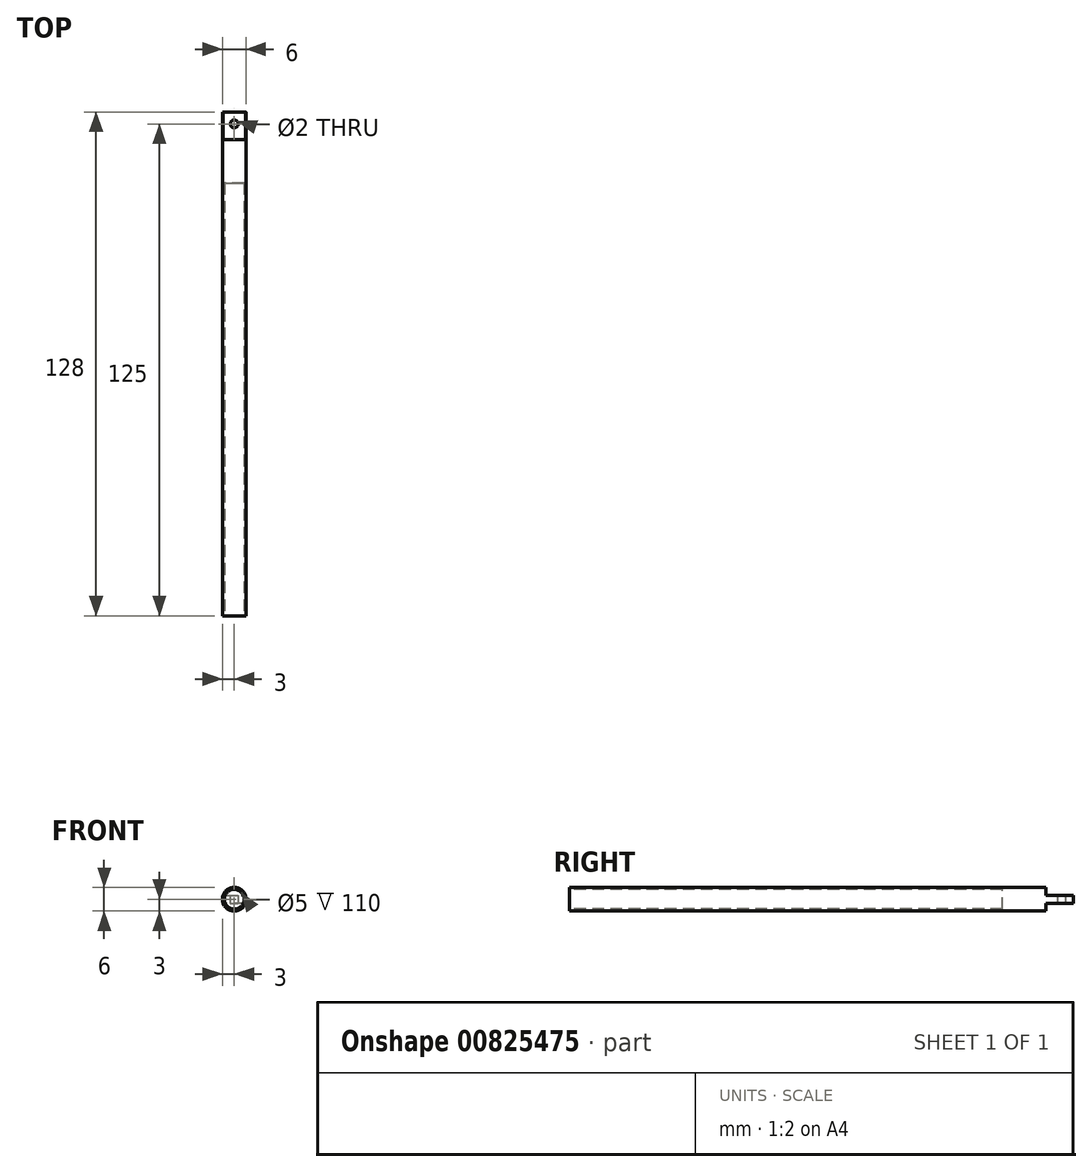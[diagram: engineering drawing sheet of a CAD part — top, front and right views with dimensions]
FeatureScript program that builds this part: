
annotation { "Feature Type Name" : "Feature", "Feature Type Description" : "" }
export const myFeature = defineFeature(function(context is Context, id is Id, definition is map)
    precondition{}
    {
        {
            var Q0;
            Q0=qCreatedBy(makeId("Front.planeOp"),FACE);
            var sketch = newSketch(context, id + "F0", { "sketchPlane" : qUnion([Q0])});
            skCircle(sketch, "E0", {"center": v(0, 0) * mm, "radius": 3 * mm});
            skSolve(sketch);
        }
        {
            var Q0;
            Q0=makeQuery(id+"F0.imprint","IMPRINT",FACE,{"disambiguationData":[TD([[makeQuery(id+"F0.imprint","IMPRINT",EDGE,{"derivedFrom":sQuery(id+"F0.wireOp",EDGE,"E0")}),1.0]])]});
            extrude(context, id + "F1", {"entities" : qUnion([Q0]), "endBound" : BoundingType.SYMMETRIC, "depth" : 128 * mm, "offsetDistance" : 25 * mm});
        }
        {
            var Q0;
            Q0=makeQuery(id+"F1.opExtrude","CAP_FACE",FACE,{"disambiguationData":[OSD([sQuery(id+"F0.wireOp",EDGE,"E0")])],"isStart":false});
            var sketch = newSketch(context, id + "F2", { "sketchPlane" : qUnion([Q0])});
            skCircle(sketch, "E1", {"center": v(0, 0) * mm, "radius": 2.5 * mm});
            skSolve(sketch);
        }
        {
            var Q0;
            Q0=makeQuery(id+"F2.imprint","IMPRINT",FACE,{"disambiguationData":[TD([[makeQuery(id+"F2.imprint","IMPRINT",EDGE,{"derivedFrom":sQuery(id+"F2.wireOp",EDGE,"E1")}),1.0]])]});
            extrude(context, id + "F3", {"entities" : qUnion([Q0]), "operationType" : NewBodyOperationType.REMOVE, "oppositeDirection" : true, "depth" : 110 * mm, "offsetDistance" : 25 * mm});
        }
        {
            var Q0;
            Q0=qCreatedBy(makeId("Right.planeOp"),FACE);
            var sketch = newSketch(context, id + "F4", { "sketchPlane" : qUnion([Q0])});
            skLineSegment(sketch, "E2.top", {"start": v(64, 1) * mm, "end": v(57, 1) * mm});
            skPoint(sketch, "E2.middle", {"position": v(60.5, 0) * mm});
            skLineSegment(sketch, "E3.bottom", {"start": v(64, 1) * mm, "end": v(64.78, 1) * mm});
            skLineSegment(sketch, "E3.top", {"start": v(57, 4.4) * mm, "end": v(64.78, 4.4) * mm});
            skLineSegment(sketch, "E3.left", {"start": v(57, 1) * mm, "end": v(57, 4.4) * mm});
            skLineSegment(sketch, "E3.right", {"start": v(64.78, 1) * mm, "end": v(64.78, 4.4) * mm});
            skLineSegment(sketch, "E4.bottom", {"start": v(64, -1) * mm, "end": v(65.13, -1) * mm});
            skLineSegment(sketch, "E4.top", {"start": v(57, -4.58) * mm, "end": v(65.13, -4.58) * mm});
            skLineSegment(sketch, "E4.left", {"start": v(57, -1) * mm, "end": v(57, -4.58) * mm});
            skLineSegment(sketch, "E4.right", {"start": v(65.13, -1) * mm, "end": v(65.13, -4.58) * mm});
            skLineSegment(sketch, "E5", {"start": v(57, -1) * mm, "end": v(64, -1) * mm});
            skSolve(sketch);
        }
        {
            var Q0;
            Q0 = qSketchRegion(id + "F4", true);
            extrude(context, id + "F5", {"entities" : qUnion([Q0]), "operationType" : NewBodyOperationType.REMOVE, "endBound" : BoundingType.SYMMETRIC, "depth" : 6.8 * mm, "offsetDistance" : 25 * mm});
        }
        {
            var Q0;
            Q0=makeQuery(id+"F5.boolean.opBoolean","COPY",FACE,{"derivedFrom":makeQuery(id+"F5.opExtrude","SWEPT_FACE",FACE,{"disambiguationData":[OSD([sQuery(id+"F4.wireOp",EDGE,"E4.bottom"),sQuery(id+"F4.wireOp",EDGE,"E5")])]})});
            var sketch = newSketch(context, id + "F6", { "sketchPlane" : qUnion([Q0])});
            skCircle(sketch, "E6", {"center": v(0, -61) * mm, "radius": 1 * mm});
            skSolve(sketch);
        }
        {
            var Q0;
            Q0 = qSketchRegion(id + "F6", true);
            extrude(context, id + "F7", {"entities" : qUnion([Q0]), "operationType" : NewBodyOperationType.REMOVE, "oppositeDirection" : true, "depth" : 2.8 * mm, "offsetDistance" : 25 * mm});
        }
    });
